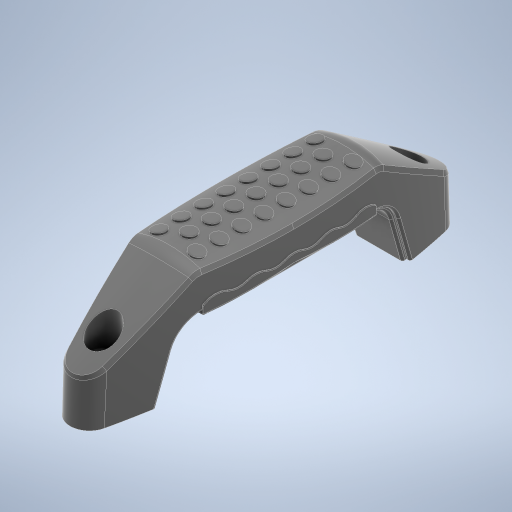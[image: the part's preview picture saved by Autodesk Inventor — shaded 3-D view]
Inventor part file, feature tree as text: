
AUTODESK INVENTOR PART (.ipt)
format: ipt  version: 2024 (Build 280153000, 153)  size: 1,647,616 bytes
history: native  units: in
note: dims shown in document units (in); Inventor stores cm internally (conversion verified against a paired STEP export)
features: other x24, mirror x1
ambient origin geometry x8: Origin, YZ Plane, XZ Plane, XY Plane, X Axis, Y Axis, Z Axis, Center Point
bodies: Solid1 (feature_tree), Solid2 (feature_tree), Solid3 (feature_tree), Solid4 (feature_tree), Solid5 (feature_tree), Solid6 (feature_tree), Solid7 (feature_tree), Solid8 (feature_tree), Solid9 (feature_tree), Solid10 (feature_tree), Solid11 (feature_tree), Solid12 (feature_tree), Solid13 (feature_tree), Solid14 (feature_tree), Solid15 (feature_tree), Solid16 (feature_tree), Solid17 (feature_tree), Solid18 (feature_tree), Solid19 (feature_tree), Solid20 (feature_tree), Solid21 (feature_tree), Solid22 (feature_tree), Solid23 (feature_tree), Solid24 (feature_tree), Solid25 (feature_tree)
feature tree (25):
  mirror  "Mirror2"
  other  "Split1[1]"
  other  "Split1[2]"
  other  "Split1[3]"
  other  "Split1[4]"
  other  "Split1[5]"
  other  "Split1[6]"
  other  "Split1[7]"
  other  "Split1[8]"
  other  "Split1[9]"
  other  "Split1[10]"
  other  "Split1[11]"
  other  "Split1[12]"
  other  "Split1[13]"
  other  "Split1[14]"
  other  "Split1[15]"
  other  "Split1[16]"
  other  "Split1[17]"
  other  "Split1[18]"
  other  "Split1[19]"
  other  "Split1[20]"
  other  "Split1[21]"
  other  "Split1[22]"
  other  "Split1[23]"
  other  "Split1[24]"
